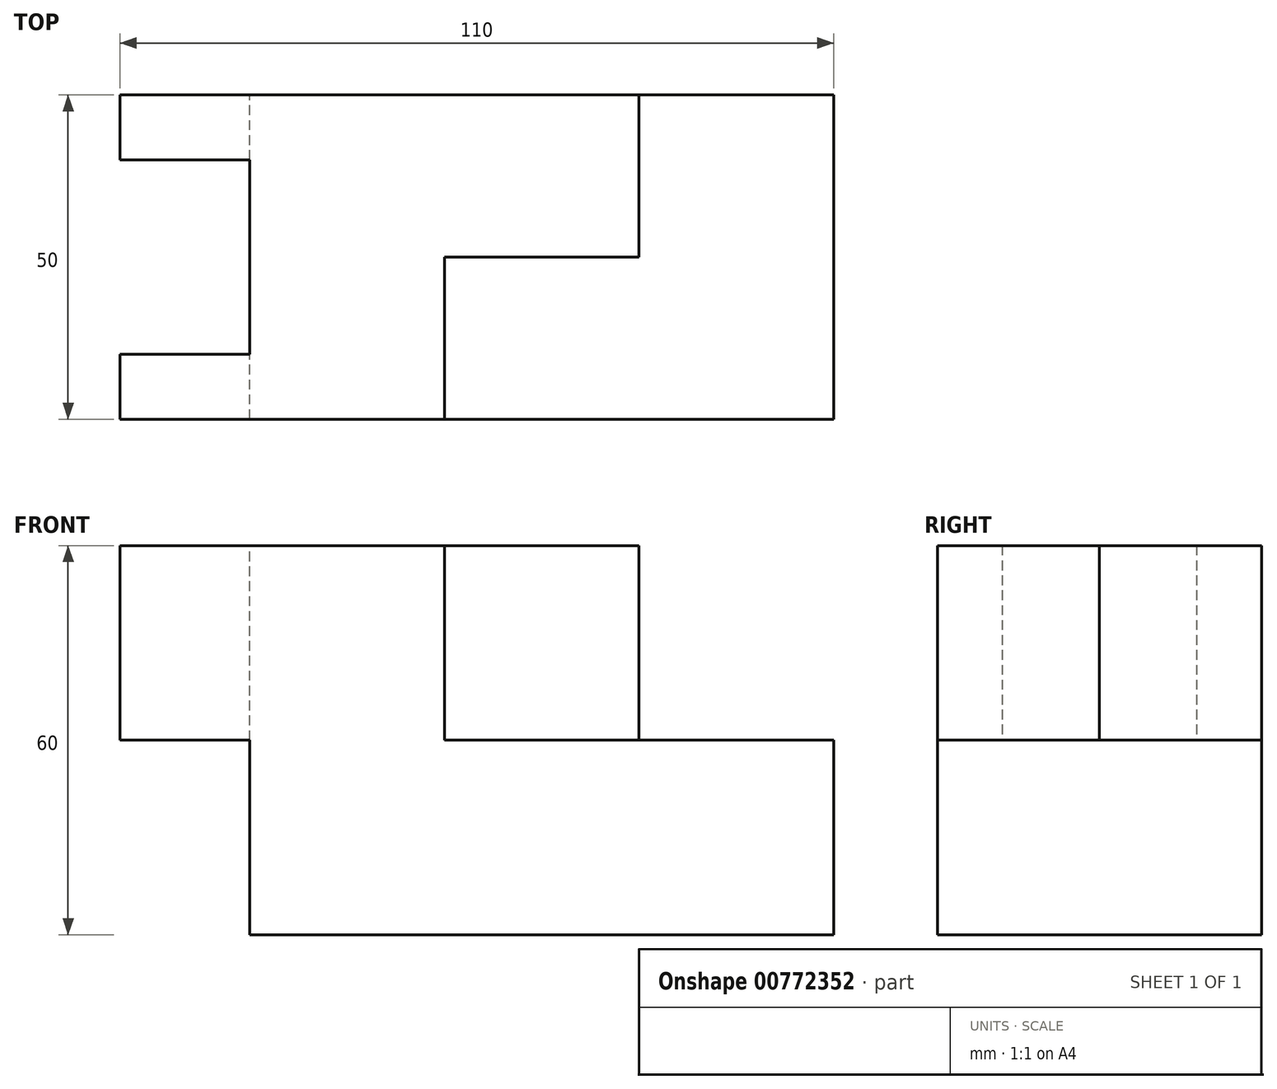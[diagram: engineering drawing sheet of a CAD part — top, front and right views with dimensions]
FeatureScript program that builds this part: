
annotation { "Feature Type Name" : "Feature", "Feature Type Description" : "" }
export const myFeature = defineFeature(function(context is Context, id is Id, definition is map)
    precondition{}
    {
        {
            var Q0;
            Q0=qCreatedBy(makeId("Front.planeOp"),FACE);
            var sketch = newSketch(context, id + "F0", { "sketchPlane" : qUnion([Q0])});
            skLineSegment(sketch, "E0", {"start": v(0, 60) * mm, "end": v(0, 30) * mm});
            skLineSegment(sketch, "E1", {"start": v(0, 30) * mm, "end": v(20, 30) * mm});
            skLineSegment(sketch, "E2", {"start": v(20, 30) * mm, "end": v(20, 0) * mm});
            skLineSegment(sketch, "E3", {"start": v(20, 0) * mm, "end": v(110, 0) * mm});
            skLineSegment(sketch, "E4", {"start": v(110, 0) * mm, "end": v(110, 30) * mm});
            skLineSegment(sketch, "E5", {"start": v(110, 30) * mm, "end": v(50, 30) * mm});
            skLineSegment(sketch, "E6", {"start": v(50, 30) * mm, "end": v(50, 60) * mm});
            skLineSegment(sketch, "E7", {"start": v(50, 60) * mm, "end": v(0, 60) * mm});
            skLineSegment(sketch, "E8", {"start": v(50, 60) * mm, "end": v(80, 60) * mm});
            skLineSegment(sketch, "E9", {"start": v(80, 60) * mm, "end": v(80, 30) * mm});
            skLineSegment(sketch, "E10", {"start": v(20, 30) * mm, "end": v(20, 60) * mm});
            skSolve(sketch);
        }
        {
            var Q0;
            Q0=qSketchRegion(id+"F0",true);
            extrude(context, id + "F1", {"entities" : qUnion([Q0]), "endBound" : BoundingType.SYMMETRIC, "depth" : 50 * mm, "offsetDistance" : 25 * mm});
        }
        {
            var Q0;
            {var subQ0=sQuery(id+"F0.wireOp",EDGE,"E0");Q0=makeQuery(id+"F0.imprint","IMPRINT",FACE,{"disambiguationData":[TD([[makeQuery(id+"F0.imprint","IMPRINT",EDGE,{"derivedFrom":subQ0}),1.0]])]});}
            extrude(context, id + "F2", {"entities" : qUnion([Q0]), "operationType" : NewBodyOperationType.REMOVE, "endBound" : BoundingType.SYMMETRIC, "oppositeDirection" : true, "depth" : 30 * mm, "offsetDistance" : 25 * mm});
        }
        {
            var Q0;
            {var subQ0=sQuery(id+"F0.wireOp",EDGE,"E6");Q0=makeQuery(id+"F0.imprint","IMPRINT",FACE,{"disambiguationData":[TD([[makeQuery(id+"F0.imprint","IMPRINT",EDGE,{"derivedFrom":subQ0}),-1.0]])]});}
            extrude(context, id + "F3", {"entities" : qUnion([Q0]), "operationType" : NewBodyOperationType.REMOVE, "endBound" : BoundingType.UP_TO_NEXT, "depth" : 25 * mm, "offsetDistance" : 25 * mm});
        }
    });
